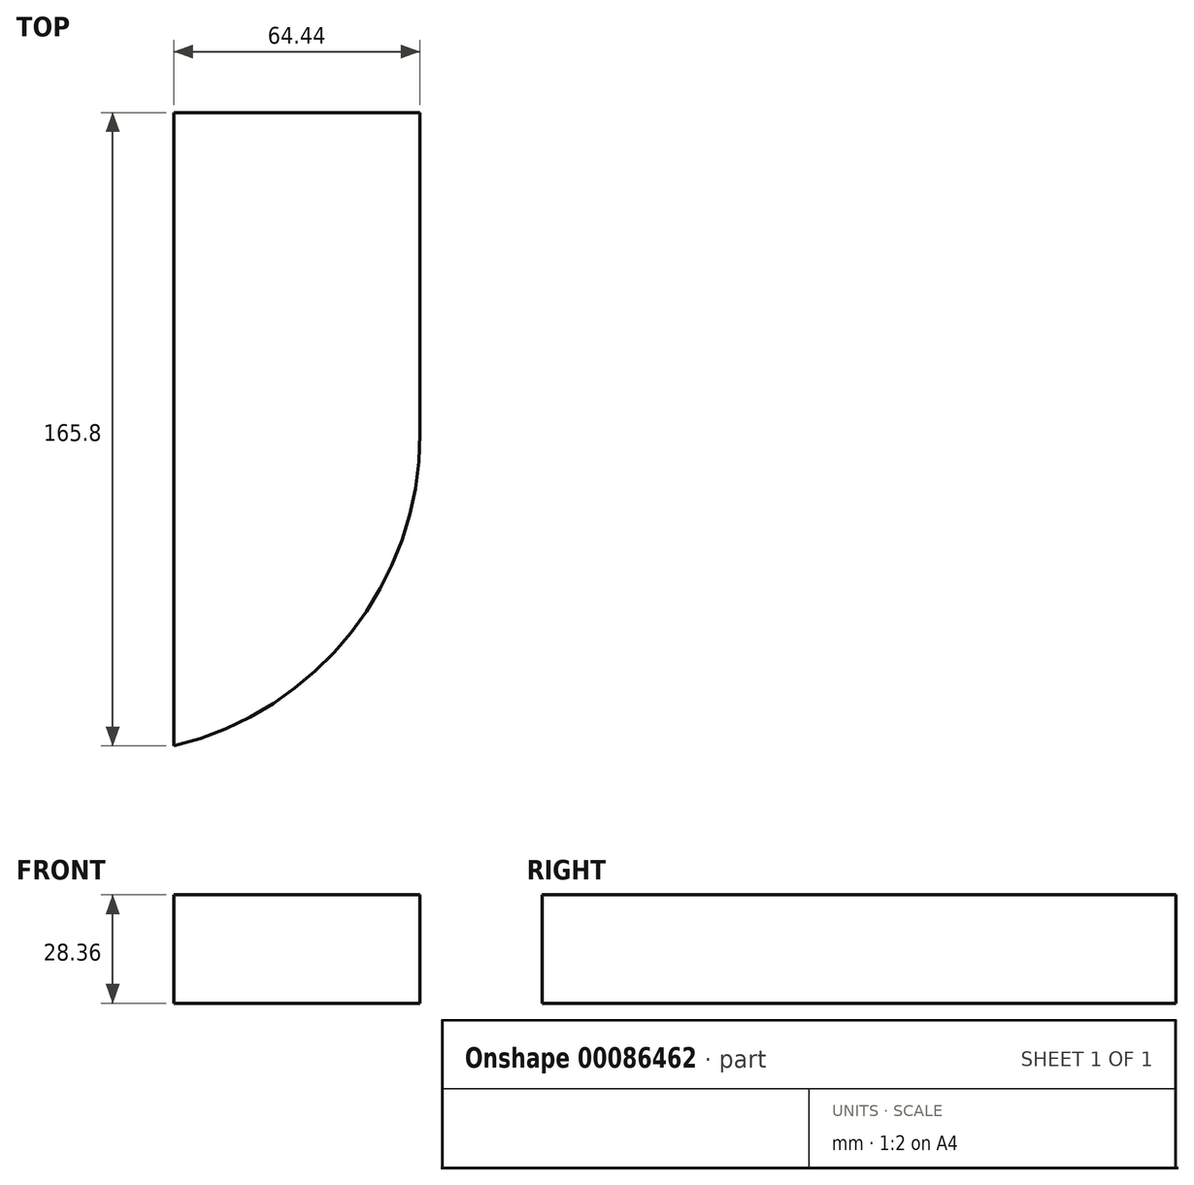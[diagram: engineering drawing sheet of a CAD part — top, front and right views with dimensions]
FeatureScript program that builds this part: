
annotation { "Feature Type Name" : "Feature", "Feature Type Description" : "" }
export const myFeature = defineFeature(function(context is Context, id is Id, definition is map)
    precondition{}
    {
        {
            var Q0;
            Q0=qCreatedBy(makeId("Front.planeOp"),FACE);
            var sketch = newSketch(context, id + "F0", { "sketchPlane" : qUnion([Q0])});
            skLineSegment(sketch, "E0.bottom", {"start": v(32.22, -14.18) * mm, "end": v(-32.22, -14.18) * mm});
            skLineSegment(sketch, "E0.top", {"start": v(32.22, 14.18) * mm, "end": v(-32.22, 14.18) * mm});
            skLineSegment(sketch, "E0.left", {"start": v(32.22, -14.18) * mm, "end": v(32.22, 14.18) * mm});
            skLineSegment(sketch, "E0.right", {"start": v(-32.22, -14.18) * mm, "end": v(-32.22, 14.18) * mm});
            skPoint(sketch, "E0.middle", {"position": v(0, 0) * mm});
            skSolve(sketch);
        }
        {
            var Q0;
            Q0=makeQuery(id+"F0.imprint","IMPRINT",FACE,{"disambiguationData":[TD([[makeQuery(id+"F0.imprint","IMPRINT",EDGE,{"derivedFrom":sQuery(id+"F0.wireOp",EDGE,"E0.bottom")}),-1.0]])]});
            extrude(context, id + "F1", {"entities" : qUnion([Q0]), "depth" : 165.8 * mm});
        }
        {
            var Q0;
            Q0=makeQuery(id+"F1.opExtrude","CAP_EDGE",EDGE,{"disambiguationData":[OSD([sQuery(id+"F0.wireOp",EDGE,"E0.left")])],"isStart":false});
            fillet(context, id + "F2", {"entities" : qUnion([Q0]), "radius" : 83.95 * mm, "tangentPropagation" : true, "allowEdgeOverflow" : false});
        }
    });
